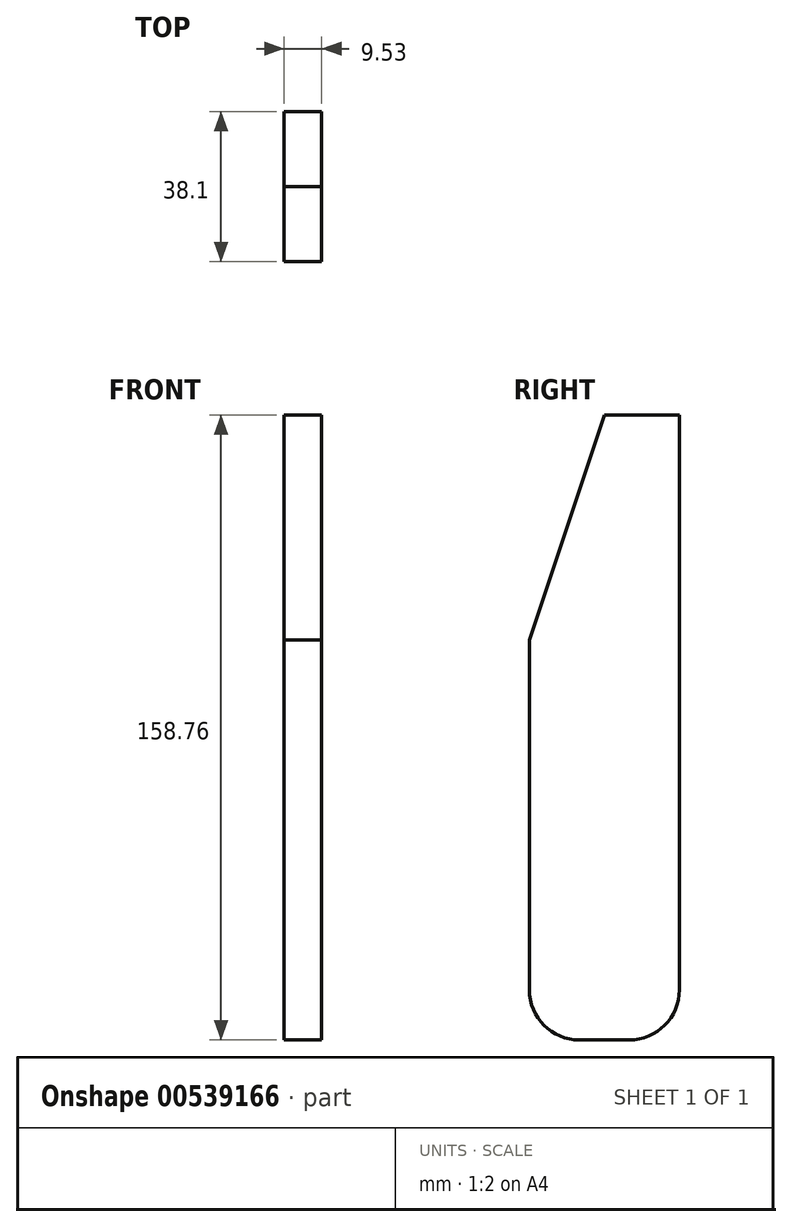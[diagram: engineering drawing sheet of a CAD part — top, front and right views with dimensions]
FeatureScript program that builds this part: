
annotation { "Feature Type Name" : "Feature", "Feature Type Description" : "" }
export const myFeature = defineFeature(function(context is Context, id is Id, definition is map)
    precondition{}
    {
        {
            var Q0;
            Q0=qCreatedBy(makeId("Right.planeOp"),FACE);
            var sketch = newSketch(context, id + "F0", { "sketchPlane" : qUnion([Q0])});
            skLineSegment(sketch, "E0.top", {"start": v(-19.05, -79.38) * mm, "end": v(19.05, -79.38) * mm});
            skLineSegment(sketch, "E0.right", {"start": v(19.05, 79.38) * mm, "end": v(19.05, -79.38) * mm});
            skPoint(sketch, "E0.middle", {"position": v(0, 0) * mm});
            skLineSegment(sketch, "E1", {"start": v(-19.05, -79.38) * mm, "end": v(-19.05, 22.23) * mm});
            skLineSegment(sketch, "E2", {"start": v(19.05, 79.38) * mm, "end": v(0, 79.38) * mm});
            skLineSegment(sketch, "E3", {"start": v(0, 79.38) * mm, "end": v(-19.05, 22.23) * mm});
            skSolve(sketch);
        }
        {
            var Q0;
            Q0=makeQuery(id+"F0.imprint","IMPRINT",FACE,{"disambiguationData":[TD([[makeQuery(id+"F0.imprint","IMPRINT",EDGE,{"derivedFrom":sQuery(id+"F0.wireOp",EDGE,"E0.top")}),1.0]])]});
            var Q1;
            Q1 = qSketchRegion(id + "FaDA2oJSuCqFV0T_1", true);
            extrude(context, id + "F1", {"entities" : qUnion([Q0, Q1]), "depth" : 9.52 * mm, "offsetDistance" : 25.4 * mm});
        }
        {
            var Q0;
            Q0=makeQuery(id+"F1.opExtrude","SWEPT_EDGE",EDGE,{"disambiguationData":[OSD([sQuery(id+"F0.wireOp",EDGE,"E0.top"),sQuery(id+"F0.wireOp",EDGE,"E1")])]});
            var Q1;
            Q1=makeQuery(id+"F1.opExtrude","SWEPT_EDGE",EDGE,{"disambiguationData":[OSD([sQuery(id+"F0.wireOp",EDGE,"E0.top"),sQuery(id+"F0.wireOp",EDGE,"E0.right")])]});
            fillet(context, id + "F2", {"entities" : qUnion([Q0, Q1]), "radius" : 12.7 * mm, "tangentPropagation" : true, "allowEdgeOverflow" : false});
        }
    });
